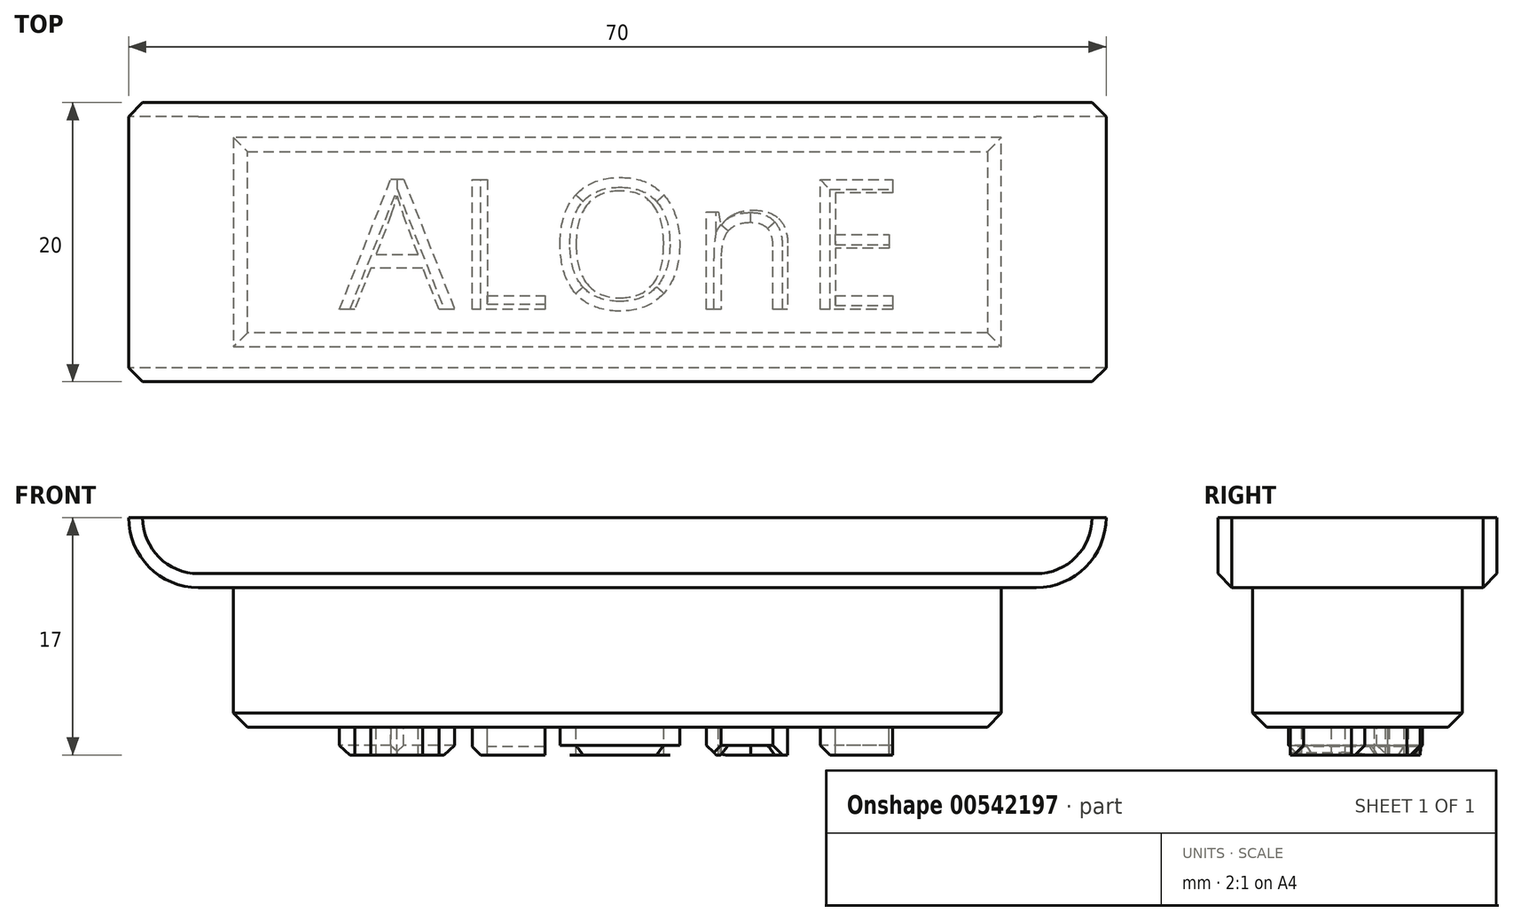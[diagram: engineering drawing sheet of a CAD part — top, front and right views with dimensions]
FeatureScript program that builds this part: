
annotation { "Feature Type Name" : "Feature", "Feature Type Description" : "" }
export const myFeature = defineFeature(function(context is Context, id is Id, definition is map)
    precondition{}
    {
        {
            var Q0;
            Q0=qCreatedBy(makeId("Top.planeOp"),FACE);
            var sketch = newSketch(context, id + "F0", { "sketchPlane" : qUnion([Q0])});
            skLineSegment(sketch, "E0.bottom", {"start": v(-27.5, 7.5) * mm, "end": v(27.5, 7.5) * mm});
            skLineSegment(sketch, "E0.top", {"start": v(-27.5, -7.5) * mm, "end": v(27.5, -7.5) * mm});
            skLineSegment(sketch, "E0.left", {"start": v(-27.5, 7.5) * mm, "end": v(-27.5, -7.5) * mm});
            skLineSegment(sketch, "E0.right", {"start": v(27.5, 7.5) * mm, "end": v(27.5, -7.5) * mm});
            skPoint(sketch, "E0.middle", {"position": v(0, 0) * mm});
            skSolve(sketch);
        }
        {
            var Q0;
            Q0 = qSketchRegion(id + "F0", true);
            extrude(context, id + "F1", {"entities" : qUnion([Q0]), "oppositeDirection" : true, "depth" : 10 * mm, "offsetDistance" : 25 * mm});
        }
        {
            var Q0;
            Q0=qCreatedBy(makeId("Top.planeOp"),FACE);
            var sketch = newSketch(context, id + "F2", { "sketchPlane" : qUnion([Q0])});
            skText(sketch, "E1", { "text": "ALOnE", "fontName": "OpenSans-Regular.ttf"});
            const initialGuessF2  = {"E1": [-0.0199, -0.00481, 1, 0, 0.00938]};
            skSetInitialGuess(sketch, initialGuessF2);
            skSolve(sketch);
        }
        {
            var Q0;
            Q0=makeQuery(id+"F2.imprint","IMPRINT",FACE,{"disambiguationData":[TD([[makeQuery(id+"F2.imprint","IMPRINT",EDGE,{"derivedFrom":sQuery(id+"F2.wireOp",EDGE,"E1.sketch_text.stroke-13")}),-1.0]])]});
            var Q1;
            Q1=makeQuery(id+"F2.imprint","IMPRINT",FACE,{"disambiguationData":[TD([[makeQuery(id+"F2.imprint","IMPRINT",EDGE,{"derivedFrom":sQuery(id+"F2.wireOp",EDGE,"E1.sketch_text.stroke-35")}),-1.0]])]});
            var Q2;
            Q2=makeQuery(id+"F2.imprint","IMPRINT",FACE,{"disambiguationData":[TD([[makeQuery(id+"F2.imprint","IMPRINT",EDGE,{"derivedFrom":sQuery(id+"F2.wireOp",EDGE,"E1.sketch_text.stroke-52")}),-1.0]])]});
            var Q3;
            Q3=makeQuery(id+"F2.imprint","IMPRINT",FACE,{"disambiguationData":[TD([[makeQuery(id+"F2.imprint","IMPRINT",EDGE,{"derivedFrom":sQuery(id+"F2.wireOp",EDGE,"E1.sketch_text.stroke-0")}),-1.0]])]});
            var Q4;
            Q4=makeQuery(id+"F2.imprint","IMPRINT",FACE,{"disambiguationData":[TD([[makeQuery(id+"F2.imprint","IMPRINT",EDGE,{"derivedFrom":sQuery(id+"F2.wireOp",EDGE,"E1.sketch_text.stroke-19")}),-1.0]])]});
            extrude(context, id + "F3", {"entities" : qUnion([Q0, Q1, Q2, Q3, Q4]), "operationType" : NewBodyOperationType.ADD, "oppositeDirection" : true, "depth" : 12 * mm, "offsetDistance" : 25 * mm});
        }
        {
            var Q0;
            Q0=qCreatedBy(makeId("Top.planeOp"),FACE);
            var sketch = newSketch(context, id + "F4", { "sketchPlane" : qUnion([Q0])});
            skLineSegment(sketch, "E2.bottom", {"start": v(-35, 10) * mm, "end": v(35, 10) * mm});
            skLineSegment(sketch, "E2.top", {"start": v(-35, -10) * mm, "end": v(35, -10) * mm});
            skLineSegment(sketch, "E2.left", {"start": v(-35, 10) * mm, "end": v(-35, -10) * mm});
            skLineSegment(sketch, "E2.right", {"start": v(35, 10) * mm, "end": v(35, -10) * mm});
            skPoint(sketch, "E2.middle", {"position": v(0, 0) * mm});
            skSolve(sketch);
        }
        {
            var Q0;
            Q0 = qSketchRegion(id + "F4", true);
            extrude(context, id + "F5", {"entities" : qUnion([Q0]), "operationType" : NewBodyOperationType.ADD, "depth" : 5 * mm, "offsetDistance" : 25 * mm});
        }
        {
            var Q0;
            Q0=makeQuery(id+"F1.opExtrude","CAP_EDGE",EDGE,{"disambiguationData":[OSD([sQuery(id+"F0.wireOp",EDGE,"E0.top")])],"isStart":false});
            var Q1;
            Q1=makeQuery(id+"F1.opExtrude","CAP_EDGE",EDGE,{"disambiguationData":[OSD([sQuery(id+"F0.wireOp",EDGE,"E0.bottom")])],"isStart":false});
            var Q2;
            Q2=makeQuery(id+"F1.opExtrude","CAP_EDGE",EDGE,{"disambiguationData":[OSD([sQuery(id+"F0.wireOp",EDGE,"E0.left")])],"isStart":false});
            var Q3;
            Q3=makeQuery(id+"F1.opExtrude","CAP_EDGE",EDGE,{"disambiguationData":[OSD([sQuery(id+"F0.wireOp",EDGE,"E0.right")])],"isStart":false});
            chamfer(context, id + "F6", {"entities" : qUnion([Q0, Q1, Q2, Q3]), "width" : 1 * mm, "tangentPropagation" : true});
        }
        {
            var Q0;
            Q0=makeQuery(id+"F5.opExtrude","CAP_EDGE",EDGE,{"disambiguationData":[OSD([sQuery(id+"F4.wireOp",EDGE,"E2.left")])],"isStart":true});
            var Q1;
            Q1=makeQuery(id+"F5.opExtrude","CAP_EDGE",EDGE,{"disambiguationData":[OSD([sQuery(id+"F4.wireOp",EDGE,"E2.right")])],"isStart":true});
            fillet(context, id + "F7", {"entities" : qUnion([Q0, Q1]), "radius" : 5 * mm, "tangentPropagation" : true, "allowEdgeOverflow" : false});
        }
        {
            var Q0;
            Q0=makeQuery(id+"F5.opExtrude","CAP_EDGE",EDGE,{"disambiguationData":[OSD([sQuery(id+"F4.wireOp",EDGE,"E2.top")])],"isStart":true});
            var Q1;
            Q1=makeQuery(id+"F5.opExtrude","CAP_EDGE",EDGE,{"disambiguationData":[OSD([sQuery(id+"F4.wireOp",EDGE,"E2.bottom")])],"isStart":true});
            chamfer(context, id + "F8", {"entities" : qUnion([Q0, Q1]), "width" : 1 * mm, "tangentPropagation" : true});
        }
        {
            var Q0;
            Q0=makeQuery(id+"F3.opExtrude","CAP_EDGE",EDGE,{"disambiguationData":[OSD([sQuery(id+"F2.wireOp",EDGE,"E1.sketch_text.stroke-4")])],"isStart":false});
            var Q1;
            Q1=makeQuery(id+"F3.opExtrude","CAP_EDGE",EDGE,{"disambiguationData":[OSD([sQuery(id+"F2.wireOp",EDGE,"E1.sketch_text.stroke-6")])],"isStart":false});
            chamfer(context, id + "F9", {"entities" : qUnion([Q0, Q1]), "width" : 0.7 * mm, "tangentPropagation" : true});
        }
        {
            var Q0;
            Q0=makeQuery(id+"F3.opExtrude","CAP_EDGE",EDGE,{"disambiguationData":[OSD([sQuery(id+"F2.wireOp",EDGE,"E1.sketch_text.stroke-13")])],"isStart":false});
            chamfer(context, id + "F10", {"entities" : qUnion([Q0]), "width" : 0.6 * mm, "tangentPropagation" : true});
        }
        {
            var Q0;
            Q0=makeQuery(id+"F3.opExtrude","CAP_EDGE",EDGE,{"disambiguationData":[OSD([sQuery(id+"F2.wireOp",EDGE,"E1.sketch_text.stroke-16")])],"isStart":false});
            chamfer(context, id + "F11", {"entities" : qUnion([Q0]), "width" : 0.6 * mm, "tangentPropagation" : true});
        }
        {
            var Q0;
            Q0=makeQuery(id+"F3.opExtrude","CAP_EDGE",EDGE,{"disambiguationData":[OSD([sQuery(id+"F2.wireOp",EDGE,"E1.sketch_text.stroke-42")])],"isStart":false});
            var Q1;
            Q1=makeQuery(id+"F3.opExtrude","CAP_EDGE",EDGE,{"disambiguationData":[OSD([sQuery(id+"F2.wireOp",EDGE,"E1.sketch_text.stroke-35")])],"isStart":false});
            chamfer(context, id + "F12", {"entities" : qUnion([Q0, Q1]), "width" : 0.7 * mm, "tangentPropagation" : true});
        }
        {
            var Q0;
            Q0=makeQuery(id+"F3.opExtrude","CAP_EDGE",EDGE,{"disambiguationData":[OSD([sQuery(id+"F2.wireOp",EDGE,"E1.sketch_text.stroke-53")])],"isStart":false});
            chamfer(context, id + "F13", {"entities" : qUnion([Q0]), "width" : 0.7 * mm, "tangentPropagation" : true});
        }
        {
            var Q0;
            Q0=makeQuery(id+"F3.opExtrude","CAP_EDGE",EDGE,{"disambiguationData":[OSD([sQuery(id+"F2.wireOp",EDGE,"E1.sketch_text.stroke-54")])],"isStart":false});
            var Q1;
            Q1=makeQuery(id+"F3.opExtrude","CAP_EDGE",EDGE,{"disambiguationData":[OSD([sQuery(id+"F2.wireOp",EDGE,"E1.sketch_text.stroke-58")])],"isStart":false});
            var Q2;
            Q2=makeQuery(id+"F3.opExtrude","CAP_EDGE",EDGE,{"disambiguationData":[OSD([sQuery(id+"F2.wireOp",EDGE,"E1.sketch_text.stroke-62")])],"isStart":false});
            chamfer(context, id + "F14", {"entities" : qUnion([Q0, Q1, Q2]), "width" : 0.7 * mm, "tangentPropagation" : true});
        }
        {
            var Q0;
            Q0=makeQuery(id+"F3.opExtrude","CAP_EDGE",EDGE,{"disambiguationData":[OSD([sQuery(id+"F2.wireOp",EDGE,"E1.sketch_text.stroke-23")])],"isStart":false});
            chamfer(context, id + "F15", {"entities" : qUnion([Q0]), "width" : 0.7 * mm, "tangentPropagation" : true});
        }
    });
